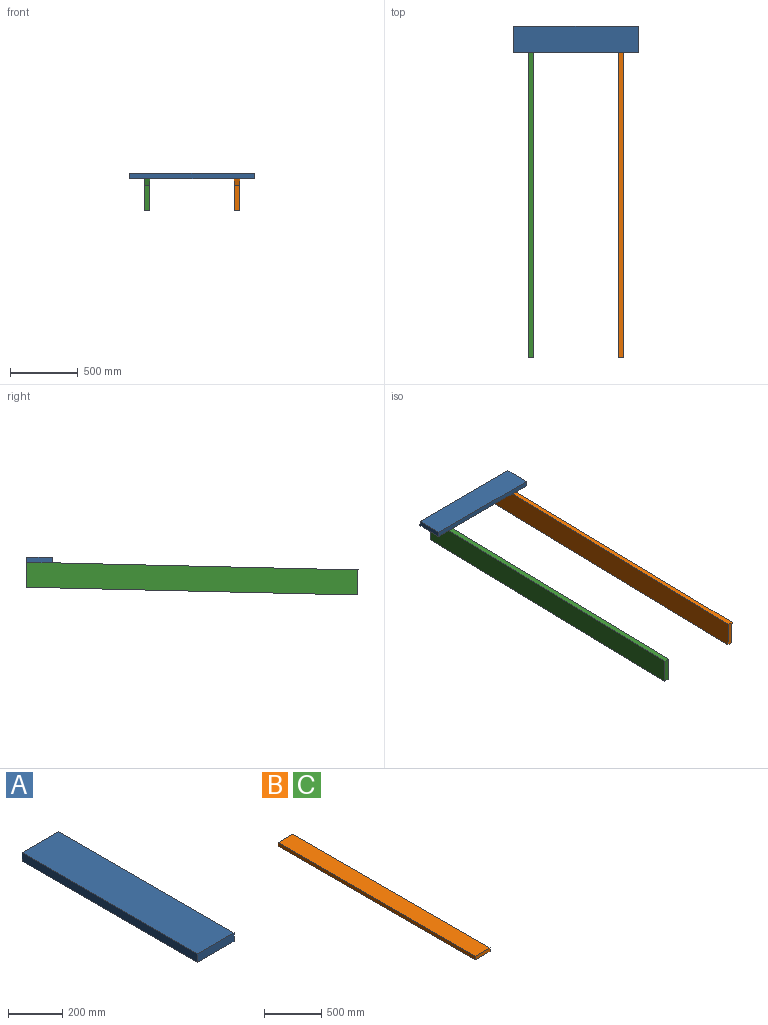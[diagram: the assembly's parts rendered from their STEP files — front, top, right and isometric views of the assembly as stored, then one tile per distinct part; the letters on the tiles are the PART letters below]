
ASSEMBLY  parts=3 mates=3
PART A: 6 faces, bbox 190.5x914.4x38.1 mm
  f0: plane 914.4x38.1mm, normal (-1,0,0), area 34838.6mm2, adj f1,f3,f4,f5
  f1: plane 190.5x38.1mm, normal (0,-1,0), area 7258mm2, adj f0,f2,f4,f5
  f2: plane 914.4x38.1mm, normal (1,0,0), area 34838.6mm2, adj f1,f3,f4,f5
  f3: plane 190.5x38.1mm, normal (0,1,0), area 7258mm2, adj f0,f2,f4,f5
  f4: plane 914.4x190.5mm, normal (0,0,1), area 174193.2mm2, adj f0,f1,f2,f3
  f5: plane 914.4x190.5mm, normal (0,0,-1), area 174193.2mm2, adj f0,f1,f2,f3
PART B: 6 faces, bbox 184.2x2438.4x38.1 mm
  f0: plane 2438.4x38.1mm, normal (-1,0,0), area 92903mm2, adj f1,f3,f4,f5
  f1: plane 184.15x38.1mm, normal (0,-1,0), area 7016.1mm2, adj f0,f2,f4,f5
  f2: plane 2438.4x38.1mm, normal (1,0,0), area 92903mm2, adj f1,f3,f4,f5
  f3: plane 184.15x38.1mm, normal (0,1,0), area 7016.1mm2, adj f0,f2,f4,f5
  f4: plane 2438.4x184.15mm, normal (0,0,1), area 449031.4mm2, adj f0,f1,f2,f3
  f5: plane 2438.4x184.15mm, normal (0,0,-1), area 449031.4mm2, adj f0,f1,f2,f3
PART C: same geometry as B
PLACE A rot(axis=(0.01,-0.01,1),90deg) t=(-1832.69,1041.61,-690.19)mm
PLACE B rot(axis=(0.01,1,0.01),90deg) t=(-1945.31,-405.7,-1173.82)mm
PLACE C rot(axis=(0.01,-1,-0.01),90deg) t=(-2567.61,-422.45,-458.97)mm
MATE parallel A.f2 <-> C.f3  axis (0,1,0.02) through (-2257.6,1204.71,-667.32)mm
MATE parallel C.f2 <-> B.f0  axis (0,-0.02,1) through (-2586.66,-14.49,-714.93)mm
MATE planar A.f5 <-> B.f0  axis (0,0.02,-1) through (-2257.6,1109.93,-688.59)mm
